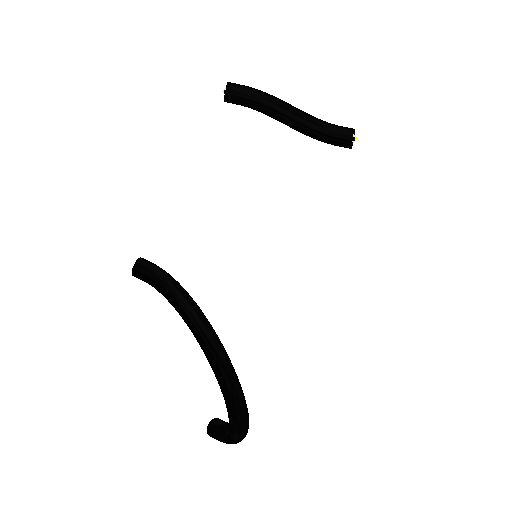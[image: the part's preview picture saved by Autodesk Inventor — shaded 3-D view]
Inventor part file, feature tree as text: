
AUTODESK INVENTOR PART (.ipt)
format: ipt  version: 2022 (Build 260153000, 153)  size: 208,384 bytes
history: native  units: mm (DEFAULTED — no unit token found)
features: other x12, plane x2, sketch x2, sweep x2
ambient origin geometry x8: Origin, YZ Plane, XZ Plane, XY Plane, X Axis, Y Axis, Z Axis, Center Point
bodies: Body1 (feature_tree), Body2 (feature_tree)
feature tree (18):
  other  "Work Point1"
  other  "Work Point2"
  other  "Wire1"
  other  "Work Point3"
  other  "Work Point4"
  other  "Wire2"
  plane  "Work Plane1"
  plane  "Work Plane2"
  other  "Work Point5"
  other  "Work Point6"
  other  "Work Point7"
  other  "Work Point8"
  sketch  "Sketch1"  dims[d0=0.0mm d1=0.0mm d2=0.0mm d3=0.0mm]
  other  "Srf1"
  sketch  "Sketch2"
  other  "Srf2"
  sweep  "SweepSrf1"
  sweep  "SweepSrf2"
